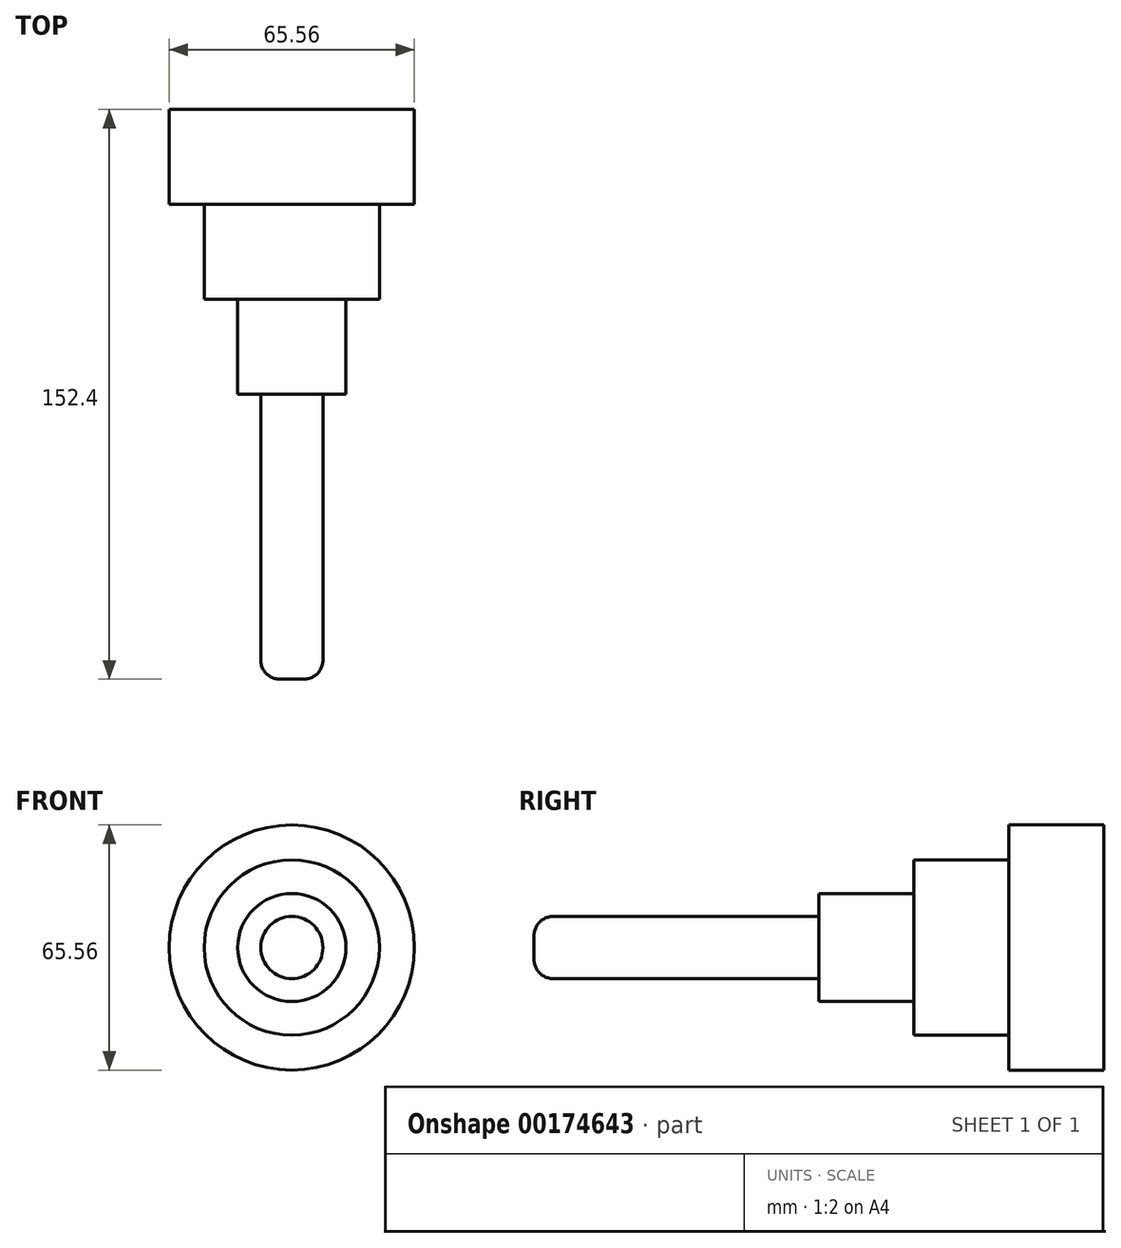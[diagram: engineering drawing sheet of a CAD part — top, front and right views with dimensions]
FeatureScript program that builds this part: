
annotation { "Feature Type Name" : "Feature", "Feature Type Description" : "" }
export const myFeature = defineFeature(function(context is Context, id is Id, definition is map)
    precondition{}
    {
        {
            var Q0;
            Q0=qCreatedBy(makeId("Front.planeOp"),FACE);
            var sketch = newSketch(context, id + "F0", { "sketchPlane" : qUnion([Q0])});
            skCircle(sketch, "E0", {"center": v(0, 0) * mm, "radius": 32.78 * mm});
            skSolve(sketch);
        }
        {
            var Q0;
            Q0=makeQuery(id+"F0.imprint","IMPRINT",FACE,{"disambiguationData":[TD([[makeQuery(id+"F0.imprint","IMPRINT",EDGE,{"derivedFrom":sQuery(id+"F0.wireOp",EDGE,"E0")}),1.0]])]});
            extrude(context, id + "F1", {"entities" : qUnion([Q0]), "depth" : 25.4 * mm});
        }
        {
            var Q0;
            Q0=makeQuery(id+"F1.opExtrude","CAP_FACE",FACE,{"disambiguationData":[OSD([sQuery(id+"F0.wireOp",EDGE,"E0")])],"isStart":false});
            var sketch = newSketch(context, id + "F2", { "sketchPlane" : qUnion([Q0])});
            skCircle(sketch, "E1", {"center": v(0, 0) * mm, "radius": 23.43 * mm});
            skSolve(sketch);
        }
        {
            var Q0;
            Q0=makeQuery(id+"F2.imprint","IMPRINT",FACE,{"disambiguationData":[TD([[makeQuery(id+"F2.imprint","IMPRINT",EDGE,{"derivedFrom":sQuery(id+"F2.wireOp",EDGE,"E1")}),1.0]])]});
            extrude(context, id + "F3", {"entities" : qUnion([Q0]), "operationType" : NewBodyOperationType.ADD, "depth" : 25.4 * mm});
        }
        {
            var Q0;
            Q0=makeQuery(id+"F3.opExtrude","CAP_FACE",FACE,{"disambiguationData":[OSD([sQuery(id+"F2.wireOp",EDGE,"E1")])],"isStart":false});
            var sketch = newSketch(context, id + "F4", { "sketchPlane" : qUnion([Q0])});
            skCircle(sketch, "E2", {"center": v(0, 0) * mm, "radius": 14.46 * mm});
            skSolve(sketch);
        }
        {
            var Q0;
            Q0 = qSketchRegion(id + "F4", true);
            extrude(context, id + "F5", {"entities" : qUnion([Q0]), "operationType" : NewBodyOperationType.ADD, "depth" : 25.4 * mm});
        }
        {
            var Q0;
            Q0=makeQuery(id+"F5.opExtrude","CAP_FACE",FACE,{"disambiguationData":[OSD([sQuery(id+"F4.wireOp",EDGE,"E2")])],"isStart":false});
            var sketch = newSketch(context, id + "F6", { "sketchPlane" : qUnion([Q0])});
            skCircle(sketch, "E3", {"center": v(0, 0) * mm, "radius": 8.3 * mm});
            skSolve(sketch);
        }
        {
            var Q0;
            Q0 = qSketchRegion(id + "F6", true);
            extrude(context, id + "F7", {"entities" : qUnion([Q0]), "operationType" : NewBodyOperationType.ADD, "depth" : 76.2 * mm});
        }
        {
            var Q0;
            Q0=makeQuery(id+"F3.opExtrude","CAP_EDGE",EDGE,{"disambiguationData":[OSD([sQuery(id+"F2.wireOp",EDGE,"E1")])],"isStart":true});
            var Q1;
            Q1=makeQuery(id+"F5.opExtrude","CAP_EDGE",EDGE,{"disambiguationData":[OSD([sQuery(id+"F4.wireOp",EDGE,"E2")])],"isStart":true});
            var Q2;
            Q2=makeQuery(id+"F7.opExtrude","CAP_EDGE",EDGE,{"disambiguationData":[OSD([sQuery(id+"F6.wireOp",EDGE,"E3")])],"isStart":true});
            var Q3;
            Q3=makeQuery(id+"F7.opExtrude","CAP_EDGE",EDGE,{"disambiguationData":[OSD([sQuery(id+"F6.wireOp",EDGE,"E3")])],"isStart":false});
            fillet(context, id + "F8", {"entities" : qUnion([Q0, Q1, Q2, Q3]), "radius" : 5.08 * mm, "tangentPropagation" : true, "allowEdgeOverflow" : false});
        }
    });
